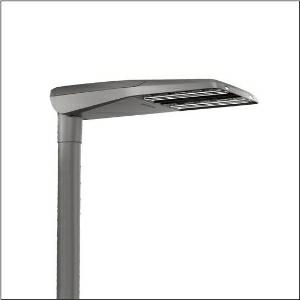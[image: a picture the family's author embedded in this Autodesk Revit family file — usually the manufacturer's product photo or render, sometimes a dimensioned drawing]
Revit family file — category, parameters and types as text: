
# Revit family: streetlight_sl_11_iq_midi___st1_2p1_0_5xc3g41e08me_f4ca
name_source: partatom
category: Lighting Fixtures
units: mm (PartAtom-declared; Revit-internal decimal feet)

## family parameters
Cut with Voids When Loaded = No
Host = Face
Light Source = No
Part Type = Normal
Room Calculation Point = No
Round Connector Dimension = Use Diameter
Shared = No

## types (1)
- --- (1 x LED, 18520 lm, 121.7 W, 4000K)
    Apparent Load = 122 VA
    CIE Flux Codes = 31 68 95 100 100
    Color Rendering = 70
    Color Temperature = 4000K
    Default Elevation = 1800 mm
    Description = Streetlight SL 11 iQ midi, mast luminaire, primary light control with 3 zone facetted reflector, of plastic, silver coated, highly specular, primary optical cover: cover, of PMMA, transparent, light distribution: ST1.2P1.0, light emission: direct distribution, primary light characteristic: asymmetric, installation type: post-top, side-entry, lamps: LED, High Power LED, rated values: 18.520lm | 121,7W | 152,2lm/W (begin service life); end service life: 18.520lm | 129W; at 50% lumin. flux: 9.260lm | 56,2W | 164,8lm/W, colour temperature: 4000K, colour rendering: CRI > 70, light colour: 740, light setting 1 begin service life: 100% | 18.520lm | 121,7W | 152,2lm/W | 4.000K, light setting 1 end service life: 129W, further light settings possible, control: optimised constant luminous flux control (CLO 2.0), Desk-Remote (wireless, voltage-free reading and setting of iQ features in the workshop via application-optimized NFC function/RFID function), Light-Fading, Smart-Wire, Night-Set, Lumen-Switch, Temp-Guard, Auto-Match, with cable H07RN-F 5x 1.5mm², mains connection: 230..240V, AC, 50/60Hz, connection cable pre-assembled, cable length: 12,5m, luminaire housing, of diecast aluminium, powder-coated, Siteco® metallic grey (DB 702S), please order mast flange separately, inclination adjustable without tools: 0°, 5°, 10°, 15° (post-top) | 0°, -5°, -10°, -15° (side-entry), sealing non-destructively replaceable, multi-level sealing system, length: 780mm, width: 376mm, height: 118mm, mast flange for spigot size: 42mm (side-entry): 5XC10008XM4, 60/48mm (side-entry/post-top): 5XC10108XM2, 76/60mm (side-entry/post-top): 5XC10108XM1, equipment: Power, protection rating (complete): IP66, insulation class (complete): insulation class II (safety insulation), certification: CE, ENEC, ENEC+, VDE, impact resistance: IK10, permissible operating ambient temperature for outdoor applications: -25..+50°C, standard-compliant lighting for roads and squares, Environmental Product Declaration (EPD) tested and certified by an independent institute, packaging unit: 1 piece

Light Distribution: ST1.2P1.0
    Height = 118 mm
    Lamp = 1 x LED
    Lamp Light Flux = 18520 lm
    Lamp Power = 121.7 W
    Lamp count = 1
    Length = 780 mm
    Luminous efficacy = 152 lm/W
    Manufacturer = Siteco
    ModVariant = No
    Model = 5XC3G41E08ME
    Number of Poles = 1
    OnlyDefault = Yes
    Power Factor = 1
    Product Name = Streetlight SL 11 iQ midi | ST1.2P1.0
    Product group = mast luminaire | pylon top
    ProductGroupID = 6100
    Protection Class = Protection class II
    Protection Degree = IP 66
    RLX_Detail_Level = 1
    RLX_Emergency_Light_Flux = 0 lm
    RLX_Emergency_Type = 0
    RLX_Emergency_Type_DB = No
    RlxData = <blob elided: 70977 chars, md5=5080d461>
    Socket = socket
    Standby Power = 0 W
    System Light Flux = 18520 lm
    System Power = 122 W
    Type Comments = factory setting: luminous flux: 100 % | dim-lin: 254 | 544 mA
    Type Image = l_1005960.jpg
    URL = http://relux.com
    VarID = @adj_037200
    Voltage = 0 V
    Weight = 0.00 kg
    Width = 376 mm

## geometry (parser evidence)
native form markers: Blend x4, Sweep x10
no freeform markers — native parametric forms only
